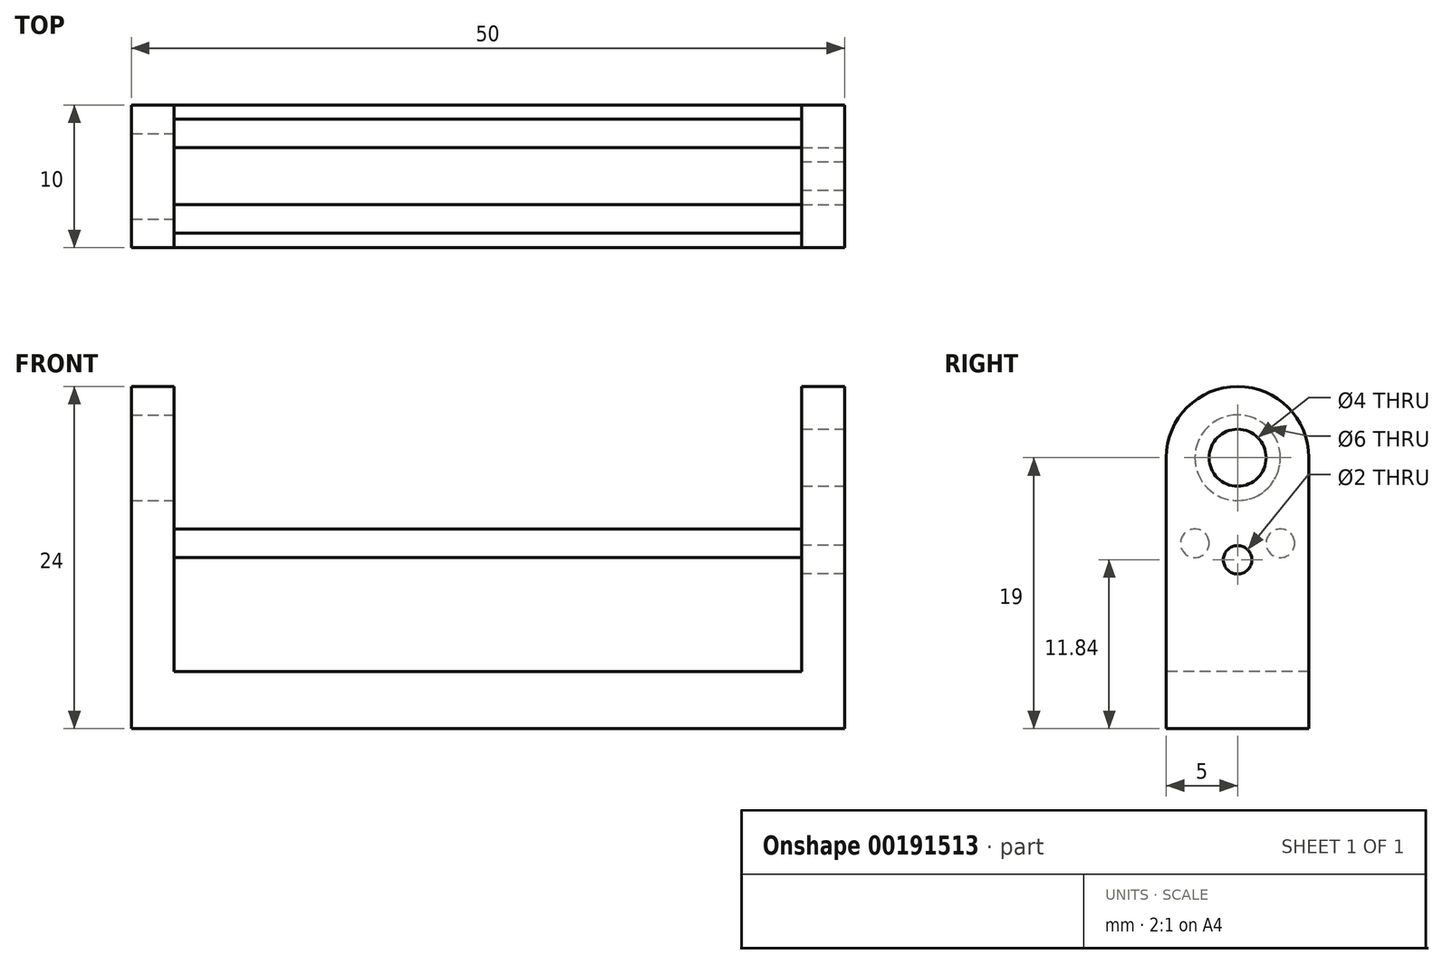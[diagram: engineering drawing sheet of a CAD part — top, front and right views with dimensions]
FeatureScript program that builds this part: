
annotation { "Feature Type Name" : "Feature", "Feature Type Description" : "" }
export const myFeature = defineFeature(function(context is Context, id is Id, definition is map)
    precondition{}
    {
        {
            var Q0;
            Q0=qCreatedBy(makeId("Top.planeOp"),FACE);
            var sketch = newSketch(context, id + "F0", { "sketchPlane" : qUnion([Q0])});
            skLineSegment(sketch, "E0.bottom", {"start": v(25, -5) * mm, "end": v(-25, -5) * mm});
            skLineSegment(sketch, "E0.top", {"start": v(25, 5) * mm, "end": v(-25, 5) * mm});
            skLineSegment(sketch, "E0.left", {"start": v(25, -5) * mm, "end": v(25, 5) * mm});
            skLineSegment(sketch, "E0.right", {"start": v(-25, -5) * mm, "end": v(-25, 5) * mm});
            skPoint(sketch, "E0.middle", {"position": v(0, 0) * mm});
            skSolve(sketch);
        }
        {
            var Q0;
            Q0 = qSketchRegion(id + "F0", true);
            extrude(context, id + "F1", {"entities" : qUnion([Q0]), "depth" : 4 * mm});
        }
        {
            var Q0;
            Q0=makeQuery(id+"F1.opExtrude","CAP_FACE",FACE,{"disambiguationData":[OSD([sQuery(id+"F0.wireOp",EDGE,"E0.bottom"),sQuery(id+"F0.wireOp",EDGE,"E0.top"),sQuery(id+"F0.wireOp",EDGE,"E0.left"),sQuery(id+"F0.wireOp",EDGE,"E0.right")])],"isStart":false});
            var sketch = newSketch(context, id + "F2", { "sketchPlane" : qUnion([Q0])});
            skLineSegment(sketch, "E1.bottom", {"start": v(25, 5) * mm, "end": v(22, 5) * mm});
            skLineSegment(sketch, "E1.top", {"start": v(25, -5) * mm, "end": v(22, -5) * mm});
            skLineSegment(sketch, "E1.left", {"start": v(25, 5) * mm, "end": v(25, -5) * mm});
            skLineSegment(sketch, "E1.right", {"start": v(22, 5) * mm, "end": v(22, -5) * mm});
            skLineSegment(sketch, "E2", {"start": v(0, 0) * mm, "end": v(0, -14.5) * mm, "construction": true});
            skLineSegment(sketch, "E3.MirrorCS", {"start": v(-25, 5) * mm, "end": v(-22, 5) * mm});
            skLineSegment(sketch, "E4.MirrorCS", {"start": v(-25, -5) * mm, "end": v(-22, -5) * mm});
            skLineSegment(sketch, "E5.MirrorCS", {"start": v(-25, 5) * mm, "end": v(-25, -5) * mm});
            skLineSegment(sketch, "E6.MirrorCS", {"start": v(-22, 5) * mm, "end": v(-22, -5) * mm});
            skSolve(sketch);
        }
        {
            var Q0;
            Q0 = qSketchRegion(id + "F2", true);
            extrude(context, id + "F3", {"entities" : qUnion([Q0]), "operationType" : NewBodyOperationType.ADD, "depth" : 20 * mm});
        }
        {
            var Q0;
            Q0=makeQuery(id+"F3.opExtrude","CAP_EDGE",EDGE,{"disambiguationData":[OSD([sQuery(id+"F2.wireOp",EDGE,"E4.MirrorCS")])],"isStart":false});
            var Q1;
            Q1=makeQuery(id+"F3.opExtrude","CAP_EDGE",EDGE,{"disambiguationData":[OSD([sQuery(id+"F2.wireOp",EDGE,"E3.MirrorCS")])],"isStart":false});
            var Q2;
            Q2=makeQuery(id+"F3.opExtrude","CAP_EDGE",EDGE,{"disambiguationData":[OSD([sQuery(id+"F2.wireOp",EDGE,"E1.top")])],"isStart":false});
            var Q3;
            Q3=makeQuery(id+"F3.opExtrude","CAP_EDGE",EDGE,{"disambiguationData":[OSD([sQuery(id+"F2.wireOp",EDGE,"E1.bottom")])],"isStart":false});
            fillet(context, id + "F4", {"entities" : qUnion([Q0, Q1, Q2, Q3]), "radius" : 5 * mm, "tangentPropagation" : true, "allowEdgeOverflow" : false});
        }
        {
            var Q0;
            Q0=makeQuery(id+"F3.boolean.opBoolean","MERGE",FACE,{"derivedFrom":[makeQuery(id+"F1.opExtrude","SWEPT_FACE",FACE,{"disambiguationData":[OSD([sQuery(id+"F0.wireOp",EDGE,"E0.left")])]}),makeQuery(id+"F3.opExtrude","SWEPT_FACE",FACE,{"disambiguationData":[OSD([sQuery(id+"F2.wireOp",EDGE,"E1.left")])]})]});
            var sketch = newSketch(context, id + "F5", { "sketchPlane" : qUnion([Q0])});
            skCircle(sketch, "E7", {"center": v(0, 19) * mm, "radius": 2 * mm});
            skSolve(sketch);
        }
        {
            var Q0;
            Q0 = qSketchRegion(id + "F5", true);
            extrude(context, id + "F6", {"entities" : qUnion([Q0]), "operationType" : NewBodyOperationType.REMOVE, "oppositeDirection" : true, "depth" : 25 * mm});
        }
        {
            var Q0;
            Q0=makeQuery(id+"F3.opExtrude","SWEPT_FACE",FACE,{"disambiguationData":[OSD([sQuery(id+"F2.wireOp",EDGE,"E6.MirrorCS")])]});
            var sketch = newSketch(context, id + "F7", { "sketchPlane" : qUnion([Q0])});
            skCircle(sketch, "E8", {"center": v(0, 19) * mm, "radius": 3 * mm});
            skSolve(sketch);
        }
        {
            var Q0;
            Q0 = qSketchRegion(id + "F7", true);
            extrude(context, id + "F8", {"entities" : qUnion([Q0]), "operationType" : NewBodyOperationType.REMOVE, "oppositeDirection" : true, "depth" : 25 * mm});
        }
        {
            var Q0;
            Q0=makeQuery(id+"F3.opExtrude","SWEPT_FACE",FACE,{"disambiguationData":[OSD([sQuery(id+"F2.wireOp",EDGE,"E6.MirrorCS")])]});
            var sketch = newSketch(context, id + "F9", { "sketchPlane" : qUnion([Q0])});
            skLineSegment(sketch, "E9", {"start": v(0, 6.78) * mm, "end": v(0, 13.12) * mm, "construction": true});
            skCircle(sketch, "E10", {"center": v(-3, 13) * mm, "radius": 1 * mm});
            skCircle(sketch, "E11", {"center": v(3, 13) * mm, "radius": 1 * mm});
            skSolve(sketch);
        }
        {
            var Q0;
            Q0 = qSketchRegion(id + "F9", true);
            extrude(context, id + "F10", {"entities" : qUnion([Q0]), "operationType" : NewBodyOperationType.ADD, "depth" : 46 * mm});
        }
        {
            var Q0;
            Q0=makeQuery(id+"F3.opExtrude","SWEPT_FACE",FACE,{"disambiguationData":[OSD([sQuery(id+"F2.wireOp",EDGE,"E1.right")])]});
            var sketch = newSketch(context, id + "F11", { "sketchPlane" : qUnion([Q0])});
            skCircle(sketch, "E12", {"center": v(0, 11.84) * mm, "radius": 1 * mm});
            skLineSegment(sketch, "E13", {"start": v(3, 13) * mm, "end": v(-4, 13) * mm, "construction": true});
            skSolve(sketch);
        }
        {
            var Q0;
            Q0 = qSketchRegion(id + "F11", true);
            extrude(context, id + "F12", {"entities" : qUnion([Q0]), "operationType" : NewBodyOperationType.REMOVE, "oppositeDirection" : true, "depth" : 25 * mm});
        }
    });
